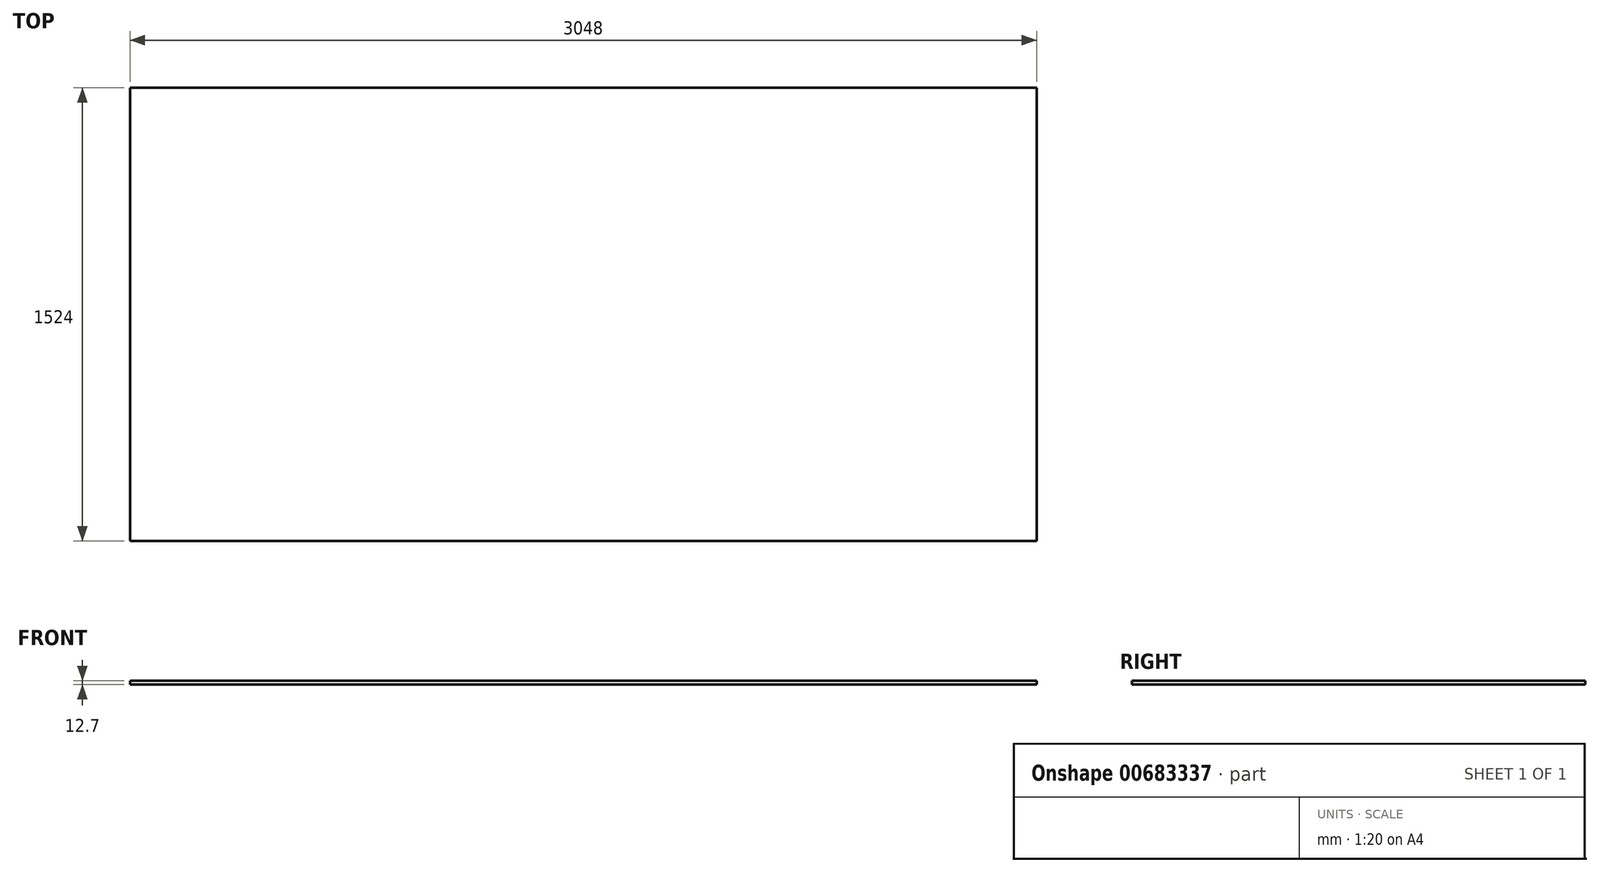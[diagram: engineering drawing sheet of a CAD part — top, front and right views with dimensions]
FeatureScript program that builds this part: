
annotation { "Feature Type Name" : "Feature", "Feature Type Description" : "" }
export const myFeature = defineFeature(function(context is Context, id is Id, definition is map)
    precondition{}
    {
        {
            var Q0;
            Q0=qCreatedBy(makeId("Top.planeOp"),FACE);
            var sketch = newSketch(context, id + "F0", { "sketchPlane" : qUnion([Q0])});
            skLineSegment(sketch, "E0.bottom", {"start": v(1524, 762) * mm, "end": v(-1524, 762) * mm});
            skLineSegment(sketch, "E0.top", {"start": v(1524, -762) * mm, "end": v(-1524, -762) * mm});
            skLineSegment(sketch, "E0.left", {"start": v(1524, 762) * mm, "end": v(1524, -762) * mm});
            skLineSegment(sketch, "E0.right", {"start": v(-1524, 762) * mm, "end": v(-1524, -762) * mm});
            skPoint(sketch, "E0.middle", {"position": v(0, 0) * mm});
            skSolve(sketch);
        }
        {
            var Q0;
            Q0=makeQuery(id+"F0.imprint","IMPRINT",FACE,{"disambiguationData":[TD([[makeQuery(id+"F0.imprint","IMPRINT",EDGE,{"derivedFrom":sQuery(id+"F0.wireOp",EDGE,"E0.bottom")}),1.0]])]});
            extrude(context, id + "F1", {"entities" : qUnion([Q0]), "depth" : 12.7 * mm, "offsetDistance" : 25 * mm});
        }
    });
